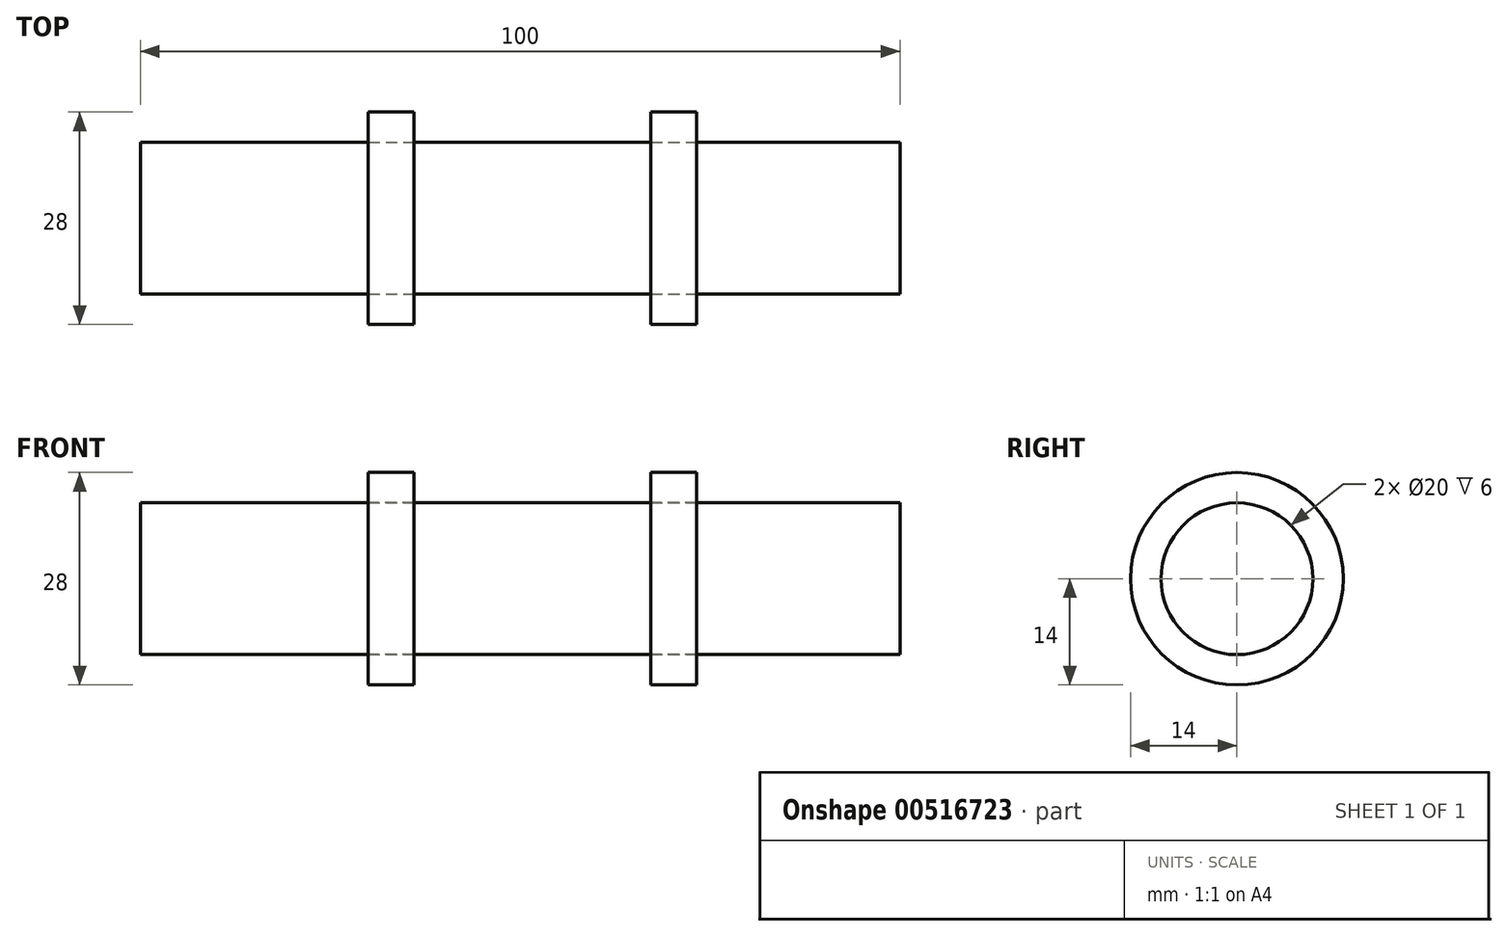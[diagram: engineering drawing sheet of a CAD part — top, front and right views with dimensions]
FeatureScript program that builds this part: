
annotation { "Feature Type Name" : "Feature", "Feature Type Description" : "" }
export const myFeature = defineFeature(function(context is Context, id is Id, definition is map)
    precondition{}
    {
        {
            var Q0;
            Q0=qCreatedBy(makeId("Front.planeOp"),FACE);
            var sketch = newSketch(context, id + "F0", { "sketchPlane" : qUnion([Q0])});
            skLineSegment(sketch, "E0", {"start": v(-22.37, 0) * mm, "end": v(24.78, 0) * mm, "construction": true});
            skLineSegment(sketch, "E1", {"start": v(0, 0) * mm, "end": v(0, 10) * mm});
            skLineSegment(sketch, "E2", {"start": v(0, 10) * mm, "end": v(100, 10) * mm});
            skLineSegment(sketch, "E3", {"start": v(100, 10) * mm, "end": v(100, 0) * mm});
            skLineSegment(sketch, "E4", {"start": v(100, 0) * mm, "end": v(0, 0) * mm});
            skLineSegment(sketch, "E5", {"start": v(30, 10) * mm, "end": v(30, 14) * mm});
            skLineSegment(sketch, "E6", {"start": v(30, 14) * mm, "end": v(36, 14) * mm});
            skLineSegment(sketch, "E7", {"start": v(36, 14) * mm, "end": v(36, 10) * mm});
            skLineSegment(sketch, "E8", {"start": v(67.2, 10) * mm, "end": v(67.2, 14) * mm});
            skLineSegment(sketch, "E9", {"start": v(67.2, 14) * mm, "end": v(73.2, 14) * mm});
            skLineSegment(sketch, "E10", {"start": v(73.2, 14) * mm, "end": v(73.2, 10) * mm});
            skSolve(sketch);
        }
        {
            var Q0;
            {var subQ4=sQuery(id+"F0.wireOp",EDGE,"E1");Q0=makeQuery(id+"F0.imprint","IMPRINT",FACE,{"disambiguationData":[TD([[makeQuery(id+"F0.imprint","IMPRINT",EDGE,{"derivedFrom":subQ4}),-1.0]])]});}
            var Q1;
            Q1=sQuery(id+"F0.wireOp",EDGE,"E0");
            revolve(context, id + "F1", {"entities" : qUnion([Q0]), "axis" : qUnion([Q1]), "revolveType" : RevolveType.FULL});
        }
        {
            var Q0;
            {var subQ0=sQuery(id+"F0.wireOp",EDGE,"E8");Q0=makeQuery(id+"F0.imprint","IMPRINT",FACE,{"disambiguationData":[TD([[makeQuery(id+"F0.imprint","IMPRINT",EDGE,{"derivedFrom":subQ0}),-1.0]])]});}
            var Q1;
            {var subQ0=sQuery(id+"F0.wireOp",EDGE,"E5");Q1=makeQuery(id+"F0.imprint","IMPRINT",FACE,{"disambiguationData":[TD([[makeQuery(id+"F0.imprint","IMPRINT",EDGE,{"derivedFrom":subQ0}),-1.0]])]});}
            var Q2;
            Q2=sQuery(id+"F0.wireOp",EDGE,"E4");
            revolve(context, id + "F2", {"entities" : qUnion([Q0, Q1]), "axis" : qUnion([Q2]), "revolveType" : RevolveType.FULL});
        }
    });
